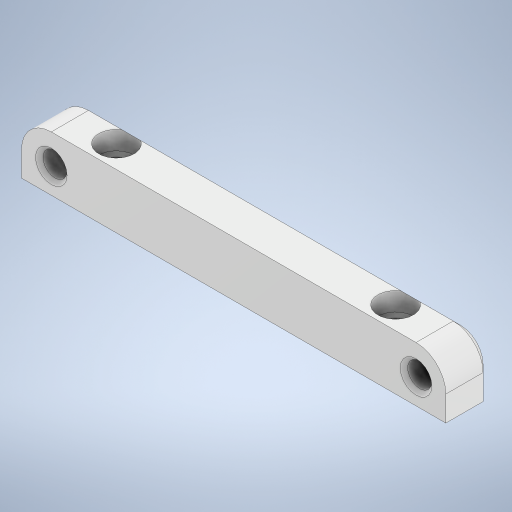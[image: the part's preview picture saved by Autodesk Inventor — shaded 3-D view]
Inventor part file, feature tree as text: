
AUTODESK INVENTOR PART (.ipt)
format: ipt  version: 2024 (Build 280153000, 153)  size: 296,448 bytes
history: native  units: mm
features: sketch x3, chamfer x2, hole x2, extrude x1, projected_geometry x1
ambient origin geometry x8: Origin, YZ Plane, XZ Plane, XY Plane, X Axis, Y Axis, Z Axis, Center Point
bodies: Solid1 (feature_tree)
feature tree (9):
  extrude  "Extrusion1"  Depth=8.25mm
  chamfer  "Chamfer2"  Distance=8.0mm
  hole  "Hole1"  [1 undecoded]
  hole  "Hole2"  [1 undecoded]
  chamfer  "Chamfer3"  Distance=75.0mm
  sketch  "Sketch1"  dims[d0=98.0mm d1=8.25mm]
  sketch  "Sketch2"  dims[d2=16.0mm]
  sketch  "Sketch3"  dims[d3=8.0mm d4=8.0mm d6=12.0mm d7=0.0mm d11=2.0mm d12=2.0mm d13=45.0deg d14=75.0mm d15=5.4mm d16=6.0mm d17=9.5mm d18=5.0mm d19=90.0deg d20=8.0mm d21=20.594885mm d24=6.5mm d25=6.0mm d26=9.5mm d27=5.0mm d28=90.0deg d29=8.0mm d30=20.594885mm d31=1.0mm d32=2.0mm d33=45.0deg d34=6.75mm]
  projected_geometry  "Projected Loop1"
note: 2 required parameter values undecoded (feature->parameter linkage not recoverable at this tier; creation-order binding heuristic only, values carry confidence <= 0.55)
